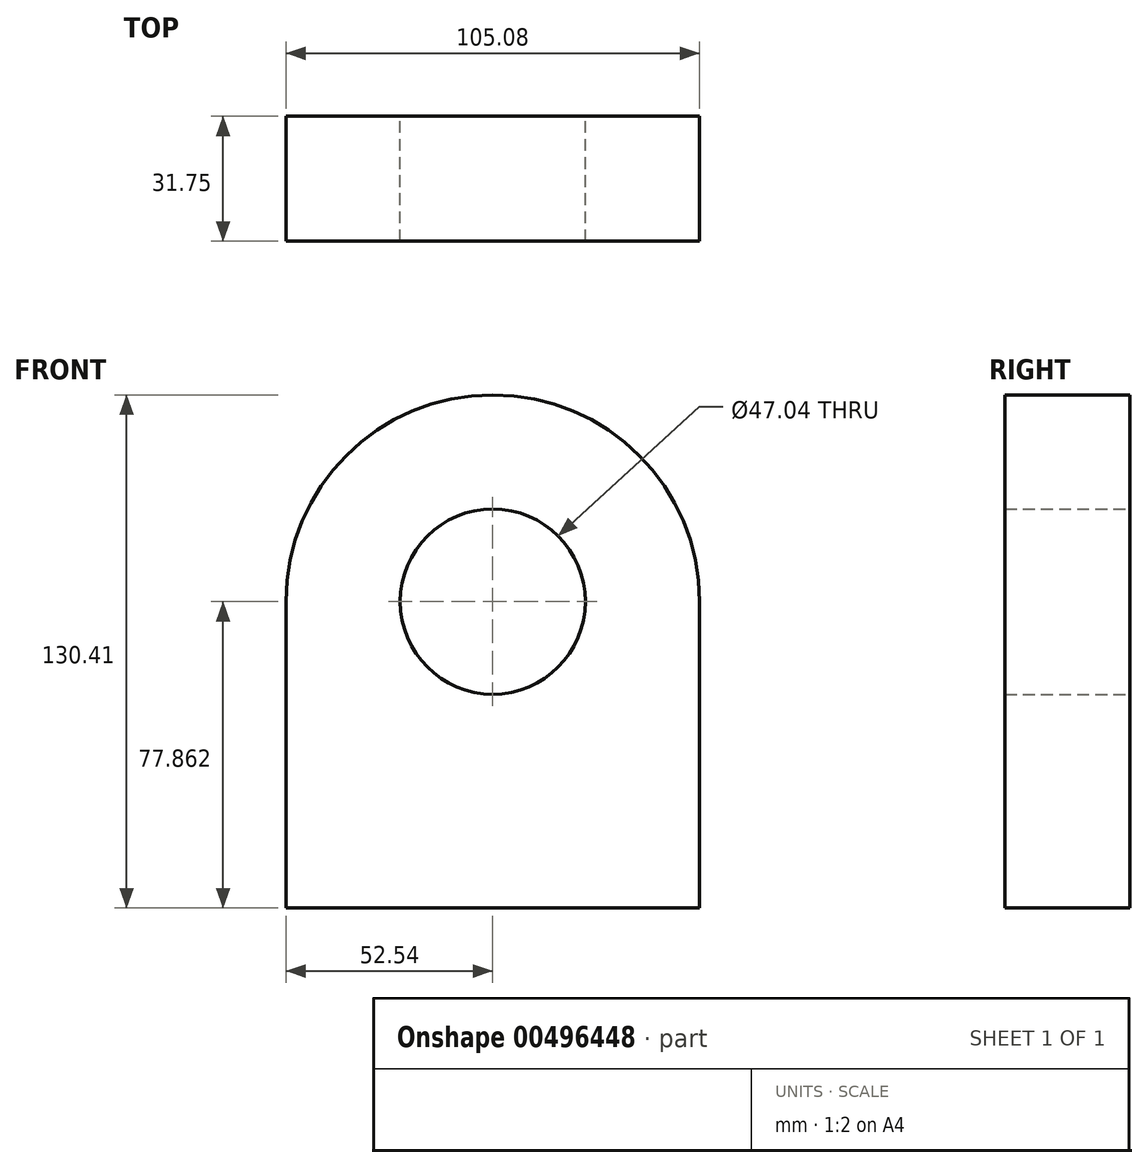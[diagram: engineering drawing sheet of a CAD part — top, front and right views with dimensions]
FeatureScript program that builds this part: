
annotation { "Feature Type Name" : "Feature", "Feature Type Description" : "" }
export const myFeature = defineFeature(function(context is Context, id is Id, definition is map)
    precondition{}
    {
        {
            var Q0;
            Q0=qCreatedBy(makeId("Front.planeOp"),FACE);
            var sketch = newSketch(context, id + "F0", { "sketchPlane" : qUnion([Q0])});
            skLineSegment(sketch, "E0.top", {"start": v(52.54, -38.93) * mm, "end": v(-52.54, -38.93) * mm});
            skLineSegment(sketch, "E0.left", {"start": v(52.54, 38.93) * mm, "end": v(52.54, -38.93) * mm});
            skLineSegment(sketch, "E0.right", {"start": v(-52.54, 38.93) * mm, "end": v(-52.54, -38.93) * mm});
            skPoint(sketch, "E0.middle", {"position": v(0, 0) * mm});
            skArc(sketch, "E1", {"start": v(52.54, 38.93) * mm, "mid": v(0, 91.48) * mm, "end": v(-52.54, 38.93) * mm});
            skCircle(sketch, "E2", {"center": v(0, 38.93) * mm, "radius": 23.52 * mm});
            skSolve(sketch);
        }
        {
            var Q0;
            Q0=makeQuery(id+"F0.imprint","IMPRINT",FACE,{"disambiguationData":[TD([[makeQuery(id+"F0.imprint","IMPRINT",EDGE,{"derivedFrom":sQuery(id+"F0.wireOp",EDGE,"E0.top")}),-1.0]])]});
            extrude(context, id + "F1", {"entities" : qUnion([Q0]), "depth" : 31.75 * mm});
        }
    });
